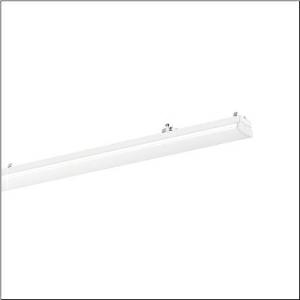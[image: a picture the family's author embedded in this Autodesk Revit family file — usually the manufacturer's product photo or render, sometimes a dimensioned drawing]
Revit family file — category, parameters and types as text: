
# Revit family: licross_r__21_recessed_opal_ho_52te1ddv4l2m_b76d
name_source: partatom
category: Lighting Fixtures
units: mm (PartAtom-declared; Revit-internal decimal feet)

## family parameters
Cut with Voids When Loaded = No
Host = Face
Light Source = No
Part Type = Normal
Room Calculation Point = No
Round Connector Dimension = Use Diameter
Shared = No

## types (1)
- --- (1 x LED, 22050 lm, 125.6 W, 4000K)
    Apparent Load = 126 VA
    CIE Flux Codes = 44 73 91 87 100
    Color Rendering = 80
    Color Temperature = 4000K
    Default Elevation = 1800 mm
    Description = Licross® 21 recessed opal HO, luminaire insert, of sheet steel, galvanised, coil coated, white, length: 2.250mm, width: 66mm, height: 67mm, LED rated luminous flux: 22.050lm, light colour: 840, control gear: DALI 2, with plug, 5-pole, with phase selection, mains connection: 220..240V, AC, 50/60Hz, rated input power: 126W, internal wiring halogen-free, primary optical cover: cover, of PMMA, light emission: direct with ceiling illumination distribution, primary light characteristic: symmetric, protection rating (complete): IP54, insulation class (complete): insulation class I (protective earthing), certification: CE, ENEC, VDE, UKCA, protection symbol: D if used in an environment with non-conductive dust loads with corresponding accessories, impact resistance: IK06, permissible ambient temperature for indoor applications: -40..+30°C, corresponds to IFS (International Featured Standards) requirements for safety and quality in the food industry, reducing of maximum allowable ambient temperature of 5°C with ceiling mounting, LABS conformity tested according to VDMA 24364:2018-05, packaging unit: 1 piece
    Height = 83 mm
    Lamp = 1 x LED
    Lamp Light Flux = 22050 lm
    Lamp Power = 125.6 W
    Lamp count = 1
    Length = 2250 mm
    Luminous efficacy = 176 lm/W
    Manufacturer = Siteco
    ModVariant = No
    Model = 52TE1DDV4L2M
    Mounting Place = Ceiling
    Mounting Type = Pendant
    Number of Poles = 1
    OnlyDefault = Yes
    Power Factor = 1
    Product Name = Licross® 21 recessed opal HO
    Product group = luminaire insert | ceiling pendant
    ProductGroupID = 902
    Protection Class = Protection class I
    Protection Degree = IP 54
    RLX_Detail_Level = 1
    RLX_Emergency_Light_Flux = 0 lm
    RLX_Emergency_Type = 0
    RLX_Emergency_Type_DB = No
    RlxData = <blob elided: 26885 chars, md5=1d5affd6>
    Socket = socket
    Standby Power = 0 W
    System Light Flux = 22050 lm
    System Power = 126 W
    Type Comments = factory setting: luminous flux: 100 % | dim-lin: 254 | 489 mA
    Type Image = l_1313666.jpg
    URL = http://relux.com
    VarID = @adj_086161
    Voltage = 0 V
    Weight = 0.00 kg
    Width = 76 mm

## geometry (parser evidence)
native form markers: Blend x4, Sweep x12
no freeform markers — native parametric forms only
